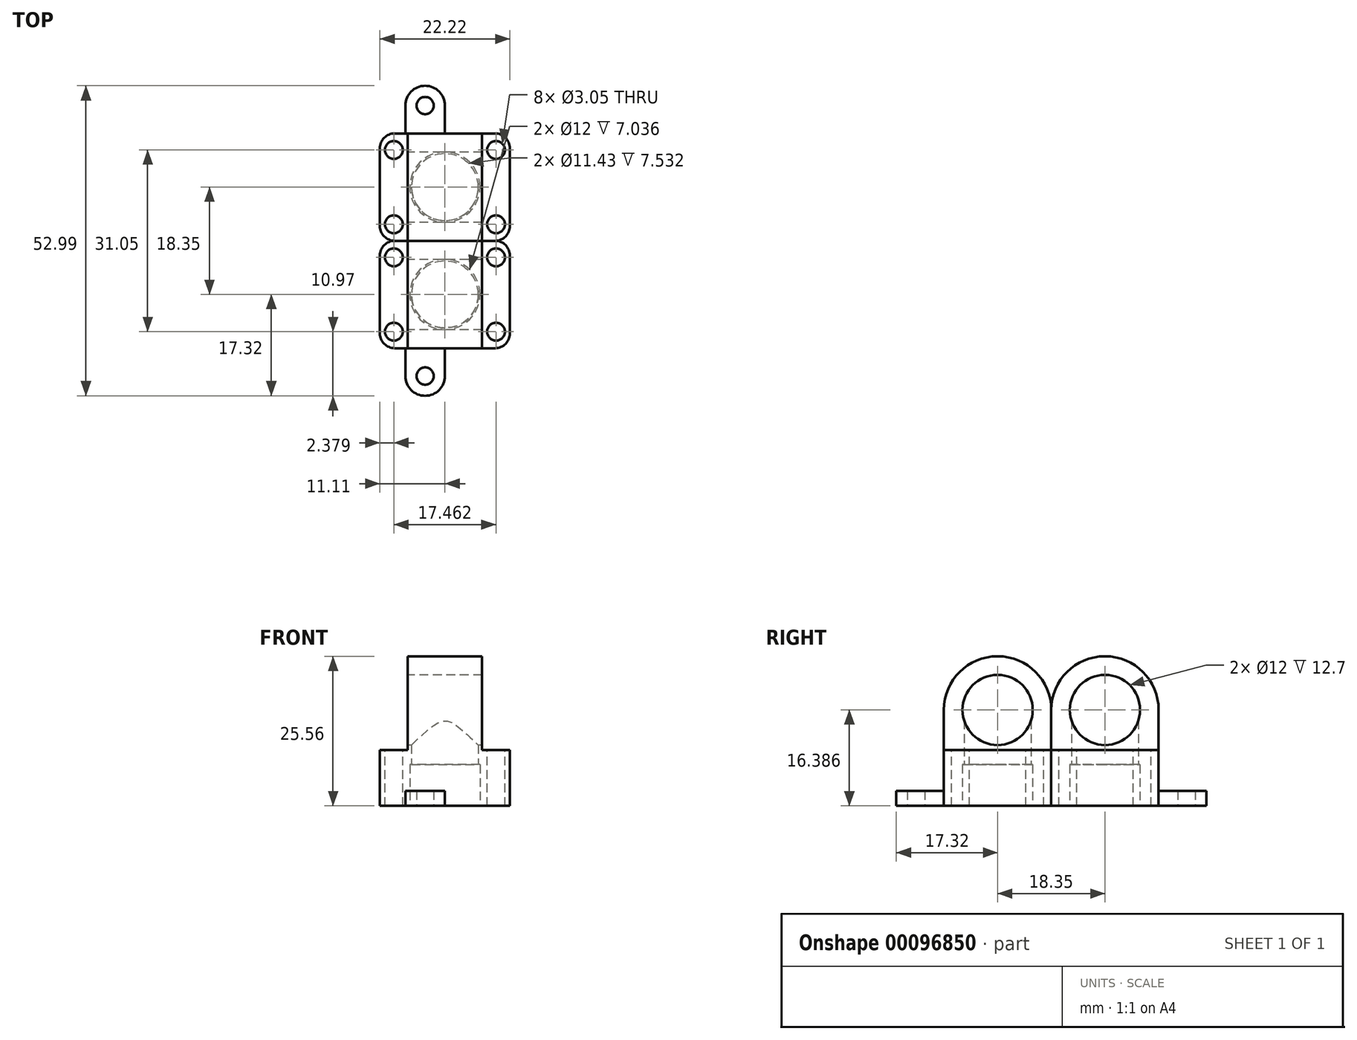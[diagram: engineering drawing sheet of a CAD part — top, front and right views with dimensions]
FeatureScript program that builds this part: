
annotation { "Feature Type Name" : "Feature", "Feature Type Description" : "" }
export const myFeature = defineFeature(function(context is Context, id is Id, definition is map)
    precondition{}
    {
        {
            var Q0;
            Q0=qCreatedBy(makeId("Top.planeOp"),FACE);
            var sketch = newSketch(context, id + "F0", { "sketchPlane" : qUnion([Q0])});
            skCircle(sketch, "E0", {"center": v(0, 0) * mm, "radius": 6 * mm});
            skArc(sketch, "E1", {"start": v(0, 9.18) * mm, "mid": v(9.18, 0) * mm, "end": v(0, -9.18) * mm});
            skLineSegment(sketch, "E2", {"start": v(0, 9.18) * mm, "end": v(-11.11, 9.18) * mm});
            skLineSegment(sketch, "E3", {"start": v(-11.11, 9.18) * mm, "end": v(-11.11, -9.18) * mm});
            skLineSegment(sketch, "E4", {"start": v(-11.11, -9.18) * mm, "end": v(0, -9.18) * mm});
            skSolve(sketch);
        }
        {
            var Q0;
            Q0=qSketchRegion(id+"F0",true);
            extrude(context, id + "F1", {"entities" : qUnion([Q0]), "depth" : 7.04 * mm});
        }
        {
            var Q0;
            Q0=makeQuery(id+"F1.opExtrude","SWEPT_FACE",FACE,{"disambiguationData":[OSD([sQuery(id+"F0.wireOp",EDGE,"E3")])]});
            var sketch = newSketch(context, id + "F2", { "sketchPlane" : qUnion([Q0])});
            skCircle(sketch, "E5", {"center": v(0, 17.8) * mm, "radius": 6 * mm});
            skArc(sketch, "E6", {"start": v(-9.17, 17.8) * mm, "mid": v(0, 26.97) * mm, "end": v(9.17, 17.8) * mm});
            skLineSegment(sketch, "E7", {"start": v(-9.17, 17.8) * mm, "end": v(-9.18, 7.04) * mm});
            skLineSegment(sketch, "E8", {"start": v(-9.18, 7.04) * mm, "end": v(9.17, 7.04) * mm});
            skLineSegment(sketch, "E9", {"start": v(9.17, 7.04) * mm, "end": v(9.17, 17.8) * mm});
            skSolve(sketch);
        }
        {
            var Q0;
            Q0=makeQuery(id+"F1.opExtrude","CAP_FACE",FACE,{"disambiguationData":[OSD([sQuery(id+"F0.wireOp",EDGE,"E0"),sQuery(id+"F0.wireOp",EDGE,"E1"),sQuery(id+"F0.wireOp",EDGE,"E2"),sQuery(id+"F0.wireOp",EDGE,"E3"),sQuery(id+"F0.wireOp",EDGE,"E4")])],"isStart":true});
            var sketch = newSketch(context, id + "F3", { "sketchPlane" : qUnion([Q0])});
            skCircle(sketch, "E10", {"center": v(-3.38, 13.94) * mm, "radius": 1.47 * mm});
            skArc(sketch, "E11", {"start": v(-6.76, 13.94) * mm, "mid": v(-3.38, 17.32) * mm, "end": v(0, 13.94) * mm});
            skLineSegment(sketch, "E12", {"start": v(-6.76, 13.94) * mm, "end": v(-6.76, 9.18) * mm});
            skLineSegment(sketch, "E13", {"start": v(-6.76, 9.18) * mm, "end": v(0, 9.18) * mm});
            skLineSegment(sketch, "E14", {"start": v(0, 9.18) * mm, "end": v(0, 13.94) * mm});
            skSolve(sketch);
        }
        {
            var Q0;
            Q0=qSketchRegion(id+"F3",true);
            extrude(context, id + "F4", {"entities" : qUnion([Q0]), "operationType" : NewBodyOperationType.ADD, "oppositeDirection" : true, "depth" : 2.54 * mm});
        }
        {
            var Q0;
            Q0=makeQuery(id+"F1.opExtrude","CAP_FACE",FACE,{"disambiguationData":[OSD([sQuery(id+"F0.wireOp",EDGE,"E0"),sQuery(id+"F0.wireOp",EDGE,"E1"),sQuery(id+"F0.wireOp",EDGE,"E2"),sQuery(id+"F0.wireOp",EDGE,"E3"),sQuery(id+"F0.wireOp",EDGE,"E4")])],"isStart":false});
            var sketch = newSketch(context, id + "F5", { "sketchPlane" : qUnion([Q0])});
            skLineSegment(sketch, "E15", {"start": v(0, 9.18) * mm, "end": v(11.11, 9.18) * mm});
            skLineSegment(sketch, "E16", {"start": v(11.11, 9.18) * mm, "end": v(11.11, -9.18) * mm});
            skLineSegment(sketch, "E17", {"start": v(11.11, -9.18) * mm, "end": v(0, -9.18) * mm});
            skArc(sketch, "E18", {"start": v(0, -9.18) * mm, "mid": v(9.18, 0) * mm, "end": v(0, 9.18) * mm});
            skSolve(sketch);
        }
        {
            var Q0;
            Q0 = qSketchRegion(id + "F5", true);
            var Q1;
            Q1=makeQuery(id+"F4.boolean.opBoolean","MERGE",FACE,{"derivedFrom":[makeQuery(id+"F1.opExtrude","CAP_FACE",FACE,{"disambiguationData":[OSD([sQuery(id+"F0.wireOp",EDGE,"E0"),sQuery(id+"F0.wireOp",EDGE,"E1"),sQuery(id+"F0.wireOp",EDGE,"E2"),sQuery(id+"F0.wireOp",EDGE,"E3"),sQuery(id+"F0.wireOp",EDGE,"E4")])],"isStart":true}),makeQuery(id+"F4.opExtrude","CAP_FACE",FACE,{"disambiguationData":[OSD([sQuery(id+"F3.wireOp",EDGE,"E10"),sQuery(id+"F3.wireOp",EDGE,"E11"),sQuery(id+"F3.wireOp",EDGE,"E12"),sQuery(id+"F3.wireOp",EDGE,"E13"),sQuery(id+"F3.wireOp",EDGE,"E14")])],"isStart":true})]});
            extrude(context, id + "F6", {"entities" : qUnion([Q0]), "operationType" : NewBodyOperationType.ADD, "endBound" : BoundingType.UP_TO_SURFACE, "oppositeDirection" : true, "endBoundEntityFace" : qUnion([Q1]), "depth" : 25.4 * mm});
        }
        {
            var Q0;
            Q0=qCreatedBy(makeId("Right.planeOp"),FACE);
            var sketch = newSketch(context, id + "F7", { "sketchPlane" : qUnion([Q0])});
            skCircle(sketch, "E19", {"center": v(0, 16.39) * mm, "radius": 6 * mm});
            skArc(sketch, "E20", {"start": v(9.18, 16.39) * mm, "mid": v(0, 25.56) * mm, "end": v(-9.18, 16.39) * mm});
            skLineSegment(sketch, "E21", {"start": v(-9.17, 16.39) * mm, "end": v(-9.18, 7.04) * mm});
            skLineSegment(sketch, "E22", {"start": v(-9.18, 7.04) * mm, "end": v(9.18, 7.04) * mm});
            skLineSegment(sketch, "E23", {"start": v(9.18, 7.04) * mm, "end": v(9.18, 16.39) * mm});
            skLineSegment(sketch, "E24.bottom", {"start": v(3, 7.04) * mm, "end": v(-3, 7.04) * mm, "construction": true});
            skLineSegment(sketch, "E24.top", {"start": v(3, 13.39) * mm, "end": v(-3, 13.39) * mm, "construction": true});
            skLineSegment(sketch, "E24.left", {"start": v(3, 7.04) * mm, "end": v(3, 13.39) * mm, "construction": true});
            skLineSegment(sketch, "E24.right", {"start": v(-3, 7.04) * mm, "end": v(-3, 13.39) * mm, "construction": true});
            skPoint(sketch, "E24.middle", {"position": v(0, 10.21) * mm});
            skCircle(sketch, "E25", {"center": v(0, 16.39) * mm, "radius": 3 * mm, "construction": true});
            skSolve(sketch);
        }
        {
            var Q0;
            Q0 = qSketchRegion(id + "F7", true);
            extrude(context, id + "F8", {"entities" : qUnion([Q0]), "endBound" : BoundingType.SYMMETRIC, "depth" : 12.7 * mm});
        }
        {
            var Q0;
            Q0=makeQuery(id+"F8.opExtrude","SWEPT_FACE",FACE,{"disambiguationData":[OSD([sQuery(id+"F7.wireOp",EDGE,"E22")])]});
            var sketch = newSketch(context, id + "F9", { "sketchPlane" : qUnion([Q0])});
            skLineSegment(sketch, "E26.bottom", {"start": v(-11.11, 9.17) * mm, "end": v(11.11, 9.17) * mm});
            skLineSegment(sketch, "E26.top", {"start": v(-11.11, -9.17) * mm, "end": v(11.11, -9.17) * mm});
            skLineSegment(sketch, "E26.left", {"start": v(-11.11, 9.17) * mm, "end": v(-11.11, -9.17) * mm});
            skLineSegment(sketch, "E26.right", {"start": v(11.11, 9.17) * mm, "end": v(11.11, -9.17) * mm});
            skPoint(sketch, "E26.middle", {"position": v(0, 0) * mm});
            skSolve(sketch);
        }
        {
            var Q0;
            Q0 = qSketchRegion(id + "F9", true);
            extrude(context, id + "F10", {"entities" : qUnion([Q0]), "operationType" : NewBodyOperationType.ADD, "oppositeDirection" : true, "depth" : 2.5 * mm});
        }
        {
            var Q0;
            {var subQ0=sQuery(id+"F9.wireOp",EDGE,"E26.bottom");var subQ3=sQuery(id+"F9.wireOp",EDGE,"E26.top");var subQ4=sQuery(id+"F9.wireOp",EDGE,"E26.left");Q0=makeQuery(id+"F10.boolean.opBoolean","SPLIT",FACE,{"disambiguationData":[TD([makeQuery(id+"F10.opExtrude","SWEPT_FACE",FACE,{"disambiguationData":[OSD([subQ4])]})])],"derivedFrom":makeQuery(id+"F10.opExtrude","CAP_FACE",FACE,{"disambiguationData":[OSD([subQ0,subQ3,subQ4,sQuery(id+"F9.wireOp",EDGE,"E26.right")])],"isStart":false})});}
            var sketch = newSketch(context, id + "F11", { "sketchPlane" : qUnion([Q0])});
            skLineSegment(sketch, "E27", {"start": v(-8.73, 9.17) * mm, "end": v(-8.73, 6.35) * mm, "construction": true});
            skLineSegment(sketch, "E28.bottom", {"start": v(-8.73, 6.35) * mm, "end": v(8.73, 6.35) * mm, "construction": true});
            skLineSegment(sketch, "E28.top", {"start": v(-8.73, -6.35) * mm, "end": v(8.73, -6.35) * mm, "construction": true});
            skLineSegment(sketch, "E28.left", {"start": v(-8.73, 6.35) * mm, "end": v(-8.73, -6.35) * mm, "construction": true});
            skLineSegment(sketch, "E28.right", {"start": v(8.73, 6.35) * mm, "end": v(8.73, -6.35) * mm, "construction": true});
            skPoint(sketch, "E28.middle", {"position": v(0, 0) * mm});
            skCircle(sketch, "E29", {"center": v(-8.73, 6.35) * mm, "radius": 1.52 * mm});
            skCircle(sketch, "E30", {"center": v(-8.73, -6.35) * mm, "radius": 1.52 * mm});
            skCircle(sketch, "E31", {"center": v(8.73, -6.35) * mm, "radius": 1.52 * mm});
            skCircle(sketch, "E32", {"center": v(8.73, 6.35) * mm, "radius": 1.52 * mm});
            skCircle(sketch, "E33", {"center": v(8.73, 6.35) * mm, "radius": 2.29 * mm, "construction": true});
            skSolve(sketch);
        }
        {
            var Q0;
            Q0 = qSketchRegion(id + "F11", true);
            extrude(context, id + "F12", {"entities" : qUnion([Q0]), "operationType" : NewBodyOperationType.REMOVE, "endBound" : BoundingType.THROUGH_ALL, "oppositeDirection" : true, "depth" : 25.4 * mm});
        }
        {
            var Q0;
            Q0=makeQuery(id+"F10.opExtrude","SWEPT_EDGE",EDGE,{"disambiguationData":[OSD([sQuery(id+"F9.wireOp",EDGE,"E26.bottom"),sQuery(id+"F9.wireOp",EDGE,"E26.right")])]});
            var Q1;
            Q1=makeQuery(id+"F10.opExtrude","SWEPT_EDGE",EDGE,{"disambiguationData":[OSD([sQuery(id+"F9.wireOp",EDGE,"E26.bottom"),sQuery(id+"F9.wireOp",EDGE,"E26.left")])]});
            var Q2;
            Q2=makeQuery(id+"F10.opExtrude","SWEPT_EDGE",EDGE,{"disambiguationData":[OSD([sQuery(id+"F9.wireOp",EDGE,"E26.top"),sQuery(id+"F9.wireOp",EDGE,"E26.right")])]});
            var Q3;
            Q3=makeQuery(id+"F10.opExtrude","SWEPT_EDGE",EDGE,{"disambiguationData":[OSD([sQuery(id+"F9.wireOp",EDGE,"E26.top"),sQuery(id+"F9.wireOp",EDGE,"E26.left")])]});
            var Q4;
            Q4=makeQuery(id+"F1.opExtrude","SWEPT_EDGE",EDGE,{"disambiguationData":[OSD([sQuery(id+"F0.wireOp",EDGE,"E2"),sQuery(id+"F0.wireOp",EDGE,"E3")])]});
            var Q5;
            Q5=makeQuery(id+"F6.opExtrude","SWEPT_EDGE",EDGE,{"disambiguationData":[OSD([sQuery(id+"F5.wireOp",EDGE,"E15"),sQuery(id+"F5.wireOp",EDGE,"E16")])]});
            var Q6;
            Q6=makeQuery(id+"F6.opExtrude","SWEPT_EDGE",EDGE,{"disambiguationData":[OSD([sQuery(id+"F5.wireOp",EDGE,"E16"),sQuery(id+"F5.wireOp",EDGE,"E17")])]});
            var Q7;
            Q7=makeQuery(id+"F1.opExtrude","SWEPT_EDGE",EDGE,{"disambiguationData":[OSD([sQuery(id+"F0.wireOp",EDGE,"E3"),sQuery(id+"F0.wireOp",EDGE,"E4")])]});
            fillet(context, id + "F13", {"entities" : qUnion([Q0, Q1, Q2, Q3, Q4, Q5, Q6, Q7]), "radius" : 2.54 * mm, "tangentPropagation" : true, "allowEdgeOverflow" : false});
        }
        {
            var Q0;
            Q0=makeQuery(id+"F10.boolean.opBoolean","MERGE",FACE,{"derivedFrom":[makeQuery(id+"F8.opExtrude","SWEPT_FACE",FACE,{"disambiguationData":[OSD([sQuery(id+"F7.wireOp",EDGE,"E22")])]}),makeQuery(id+"F10.opExtrude","CAP_FACE",FACE,{"disambiguationData":[OSD([sQuery(id+"F9.wireOp",EDGE,"E26.bottom"),sQuery(id+"F9.wireOp",EDGE,"E26.top"),sQuery(id+"F9.wireOp",EDGE,"E26.left"),sQuery(id+"F9.wireOp",EDGE,"E26.right")])],"isStart":true})]});
            var sketch = newSketch(context, id + "F14", { "sketchPlane" : qUnion([Q0])});
            skCircle(sketch, "E34", {"center": v(0, 0) * mm, "radius": 5.72 * mm});
            skSolve(sketch);
        }
        {
            var Q0;
            Q0 = qSketchRegion(id + "F14", true);
            extrude(context, id + "F15", {"entities" : qUnion([Q0]), "operationType" : NewBodyOperationType.REMOVE, "endBound" : BoundingType.UP_TO_NEXT, "oppositeDirection" : true, "depth" : 25.4 * mm});
        }
        {
            var Q0;
            Q0=makeQuery(id+"F1.opExtrude","SWEPT_BODY",BODY,{"disambiguationData":[OSD([sQuery(id+"F0.wireOp",EDGE,"E0"),sQuery(id+"F0.wireOp",EDGE,"E1"),sQuery(id+"F0.wireOp",EDGE,"E2"),sQuery(id+"F0.wireOp",EDGE,"E3"),sQuery(id+"F0.wireOp",EDGE,"E4")])]});
            var Q1;
            Q1=makeQuery(id+"F8.opExtrude","SWEPT_BODY",BODY,{"disambiguationData":[OSD([sQuery(id+"F7.wireOp",EDGE,"E19"),sQuery(id+"F7.wireOp",EDGE,"E20"),sQuery(id+"F7.wireOp",EDGE,"E21"),sQuery(id+"F7.wireOp",EDGE,"E22"),sQuery(id+"F7.wireOp",EDGE,"E23")])]});
            var Q2;
            Q2=makeQuery(id+"FeltiWKGKCvlbtT_1.boolean.opBoolean","MERGE",FACE,{"derivedFrom":[makeQuery(id+"FC8TW2MyN47ePtH_1.boolean.opBoolean","MERGE",FACE,{"derivedFrom":[makeQuery(id+"F1.opExtrude","SWEPT_FACE",FACE,{"disambiguationData":[OSD([sQuery(id+"F0.wireOp",EDGE,"E2")])]}),makeQuery(id+"FC8TW2MyN47ePtH_1.opExtrude","SWEPT_FACE",FACE,{"disambiguationData":[OSD([sQuery(id+"F2.wireOp",EDGE,"E7")])]})]}),makeQuery(id+"FeltiWKGKCvlbtT_1.opExtrude","CAP_FACE",FACE,{"disambiguationData":[OSD([sQuery(id+"FoJXFF1IQi9VodQ_1.wireOp",EDGE,"BADv9P94-FekH-q6qW-Nt0h-muAZdhJqY5QK"),sQuery(id+"FoJXFF1IQi9VodQ_1.wireOp",EDGE,"YD8KbyGX-3SDk-gQUb-EbM9-0zymLiGli5nf"),sQuery(id+"FoJXFF1IQi9VodQ_1.wireOp",EDGE,"xjQTqq31-lGEv-446r-anc1-TYDgfewutVNj")])],"isStart":true})]});
            mirror(context, id + "F16", {"entities" : qUnion([Q0, Q1]), "mirrorPlane" : qUnion([Q2])});
        }
    });
